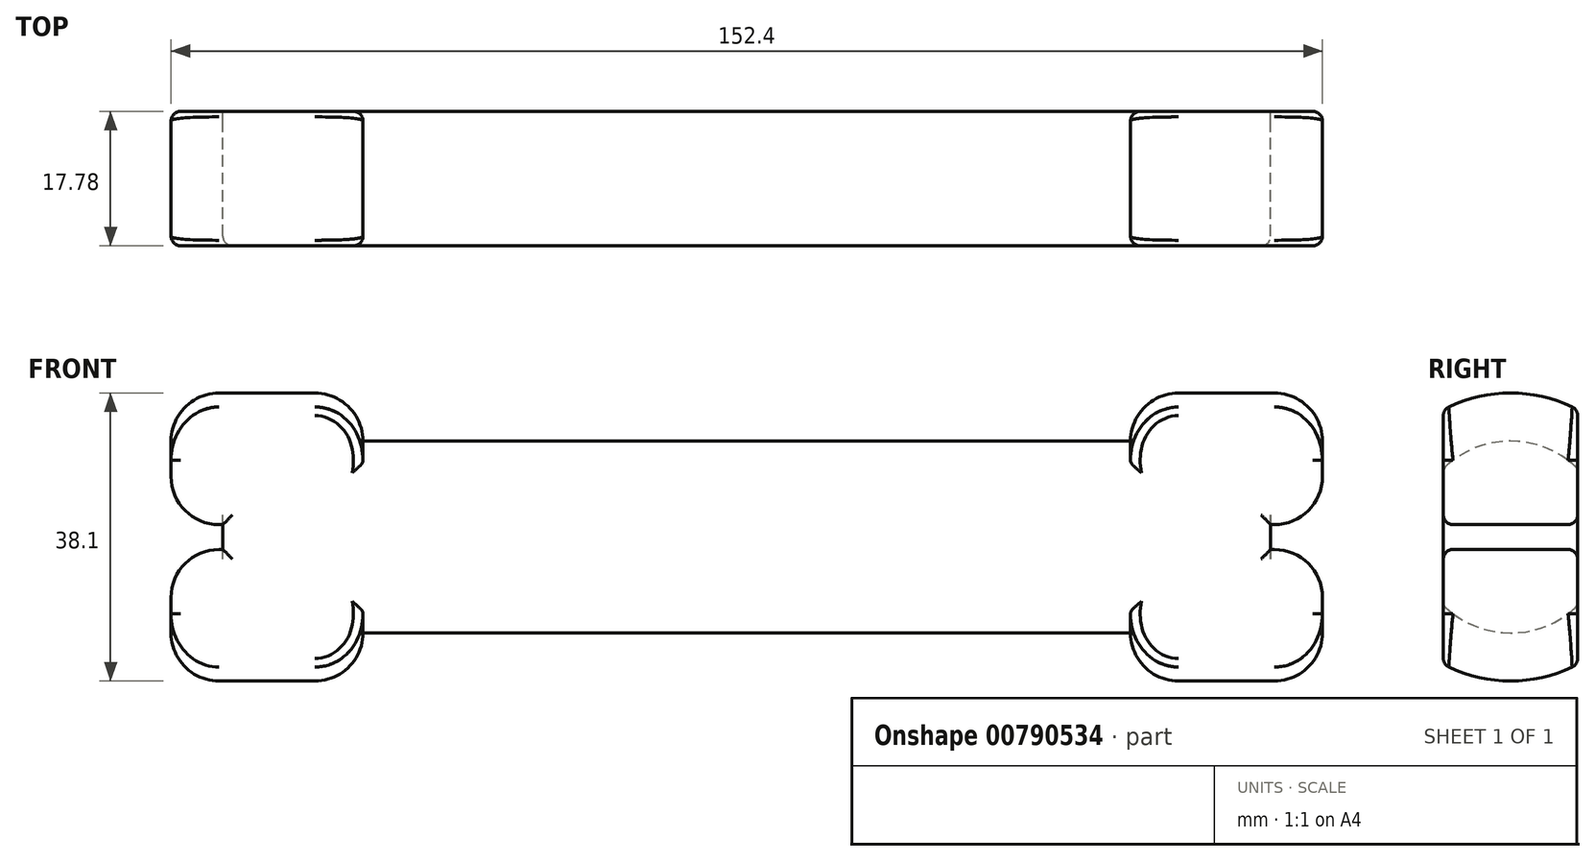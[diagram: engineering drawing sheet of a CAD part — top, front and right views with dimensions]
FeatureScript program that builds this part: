
annotation { "Feature Type Name" : "Feature", "Feature Type Description" : "" }
export const myFeature = defineFeature(function(context is Context, id is Id, definition is map)
    precondition{}
    {
        {
            var Q0;
            Q0=qCreatedBy(makeId("Front.planeOp"),FACE);
            var sketch = newSketch(context, id + "F0", { "sketchPlane" : qUnion([Q0])});
            skLineSegment(sketch, "E0.bottom", {"start": v(0, 0) * mm, "end": v(50.8, 0) * mm});
            skLineSegment(sketch, "E0.top", {"start": v(0, 19.05) * mm, "end": v(50.8, 19.05) * mm});
            skLineSegment(sketch, "E0.left", {"start": v(0, 0) * mm, "end": v(0, 19.05) * mm});
            skLineSegment(sketch, "E0.right", {"start": v(50.8, 0) * mm, "end": v(50.8, 19.05) * mm});
            skLineSegment(sketch, "E1.bottom", {"start": v(50.8, 19.05) * mm, "end": v(76.2, 19.05) * mm});
            skLineSegment(sketch, "E1.top", {"start": v(50.8, 0) * mm, "end": v(76.2, 0) * mm});
            skLineSegment(sketch, "E1.left", {"start": v(50.8, 19.05) * mm, "end": v(50.8, 0) * mm});
            skLineSegment(sketch, "E1.right", {"start": v(76.2, 19.05) * mm, "end": v(76.2, 0) * mm});
            skLineSegment(sketch, "E2.bottom", {"start": v(50.8, 19.05) * mm, "end": v(0, 19.05) * mm});
            skLineSegment(sketch, "E2.top", {"start": v(50.8, 12.7) * mm, "end": v(0, 12.7) * mm});
            skLineSegment(sketch, "E2.left", {"start": v(50.8, 19.05) * mm, "end": v(50.8, 12.7) * mm});
            skLineSegment(sketch, "E2.right", {"start": v(0, 19.05) * mm, "end": v(0, 12.7) * mm});
            skSolve(sketch);
        }
        {
            var Q0;
            {var subQ0=sQuery(id+"F0.wireOp",EDGE,"E0.bottom");Q0=makeQuery(id+"F0.imprint","IMPRINT",FACE,{"disambiguationData":[TD([[makeQuery(id+"F0.imprint","IMPRINT",EDGE,{"derivedFrom":subQ0}),1.0]])]});}
            var Q1;
            {var subQ1=sQuery(id+"F0.wireOp",EDGE,"E1.bottom");Q1=makeQuery(id+"F0.imprint","IMPRINT",FACE,{"disambiguationData":[TD([[makeQuery(id+"F0.imprint","IMPRINT",EDGE,{"derivedFrom":subQ1}),-1.0]])]});}
            var Q2;
            Q2=sQuery(id+"F0.wireOp",EDGE,"E1.top");
            revolve(context, id + "F1", {"surfaceOperationType" : NewSurfaceOperationType.NEW, "entities" : qUnion([Q0, Q1]), "axis" : qUnion([Q2]), "revolveType" : RevolveType.FULL});
        }
        {
            var Q0;
            Q0=qCreatedBy(makeId("Right.planeOp"),FACE);
            var sketch = newSketch(context, id + "F2", { "sketchPlane" : qUnion([Q0])});
            skLineSegment(sketch, "E3.bottom", {"start": v(8.89, 25.95) * mm, "end": v(35.05, 25.95) * mm});
            skLineSegment(sketch, "E3.top", {"start": v(8.9, -27.68) * mm, "end": v(35.05, -27.68) * mm});
            skLineSegment(sketch, "E3.left", {"start": v(8.89, 25.95) * mm, "end": v(8.9, -27.68) * mm});
            skLineSegment(sketch, "E3.right", {"start": v(35.05, 25.95) * mm, "end": v(35.05, -27.68) * mm});
            skSolve(sketch);
        }
        {
            var Q0;
            Q0=makeQuery(id+"F2.imprint","IMPRINT",FACE,{"disambiguationData":[TD([[makeQuery(id+"F2.imprint","IMPRINT",EDGE,{"derivedFrom":sQuery(id+"F2.wireOp",EDGE,"E3.bottom")}),-1.0]])]});
            extrude(context, id + "F3", {"entities" : qUnion([Q0]), "endBound" : BoundingType.THROUGH_ALL, "depth" : 25.4 * mm, "offsetDistance" : 25.4 * mm});
        }
        {
            var Q0;
            Q0=makeQuery(id+"F3.opExtrude","SWEPT_BODY",BODY,{"disambiguationData":[OSD([sQuery(id+"F2.wireOp",EDGE,"E3.bottom"),sQuery(id+"F2.wireOp",EDGE,"E3.top"),sQuery(id+"F2.wireOp",EDGE,"E3.left"),sQuery(id+"F2.wireOp",EDGE,"E3.right")])]});
            var Q1;
            Q1=qCreatedBy(makeId("Front.planeOp"),FACE);
            mirror(context, id + "F4", {"entities" : qUnion([Q0]), "mirrorPlane" : qUnion([Q1])});
        }
        {
            var Q0;
            Q0=makeQuery(id+"F4.opPattern","COPY",BODY,{"derivedFrom":makeQuery(id+"F3.opExtrude","SWEPT_BODY",BODY,{"disambiguationData":[OSD([sQuery(id+"F2.wireOp",EDGE,"E3.bottom"),sQuery(id+"F2.wireOp",EDGE,"E3.top"),sQuery(id+"F2.wireOp",EDGE,"E3.left"),sQuery(id+"F2.wireOp",EDGE,"E3.right")])]}),"instanceName":"1"});
            var Q1;
            Q1=makeQuery(id+"F3.opExtrude","SWEPT_BODY",BODY,{"disambiguationData":[OSD([sQuery(id+"F2.wireOp",EDGE,"E3.bottom"),sQuery(id+"F2.wireOp",EDGE,"E3.top"),sQuery(id+"F2.wireOp",EDGE,"E3.left"),sQuery(id+"F2.wireOp",EDGE,"E3.right")])]});
            var Q2;
            Q2=makeQuery(id+"F1.opRevolve","SWEPT_BODY",BODY,{"disambiguationData":[OSD([sQuery(id+"F0.wireOp",EDGE,"E0.bottom"),sQuery(id+"F0.wireOp",EDGE,"E0.left"),sQuery(id+"F0.wireOp",EDGE,"E0.right"),sQuery(id+"F0.wireOp",EDGE,"E1.bottom"),sQuery(id+"F0.wireOp",EDGE,"E1.top"),sQuery(id+"F0.wireOp",EDGE,"E1.right"),sQuery(id+"F0.wireOp",EDGE,"E2.top")])]});
            booleanBodies(context, id + "F5", {"operationType" : BooleanOperationType.SUBTRACTION, "tools" : qUnion([Q0, Q1]), "targets" : qUnion([Q2])});
        }
        {
            var Q0;
            Q0=qCreatedBy(makeId("Front.planeOp"),FACE);
            var sketch = newSketch(context, id + "F6", { "sketchPlane" : qUnion([Q0])});
            skLineSegment(sketch, "E4.bottom", {"start": v(69.35, 0) * mm, "end": v(81.98, 0) * mm});
            skLineSegment(sketch, "E4.top", {"start": v(69.35, 1.65) * mm, "end": v(81.98, 1.65) * mm});
            skLineSegment(sketch, "E4.left", {"start": v(69.35, 0) * mm, "end": v(69.35, 1.65) * mm});
            skLineSegment(sketch, "E4.right", {"start": v(81.98, 0) * mm, "end": v(81.98, 1.65) * mm});
            skLineSegment(sketch, "E5.MirrorCS", {"start": v(81.98, 0) * mm, "end": v(81.98, -1.65) * mm});
            skLineSegment(sketch, "E6.MirrorCS", {"start": v(69.35, -1.65) * mm, "end": v(81.98, -1.65) * mm});
            skLineSegment(sketch, "E7.MirrorCS", {"start": v(69.35, 0) * mm, "end": v(69.35, -1.65) * mm});
            skSolve(sketch);
        }
        {
            var Q0;
            Q0=makeQuery(id+"F6.imprint","IMPRINT",FACE,{"disambiguationData":[TD([[makeQuery(id+"F6.imprint","IMPRINT",EDGE,{"derivedFrom":sQuery(id+"F6.wireOp",EDGE,"E4.bottom")}),1.0]])]});
            var Q1;
            Q1=makeQuery(id+"F6.imprint","IMPRINT",FACE,{"disambiguationData":[TD([[makeQuery(id+"F6.imprint","IMPRINT",EDGE,{"derivedFrom":sQuery(id+"F6.wireOp",EDGE,"E4.bottom")}),-1.0]])]});
            extrude(context, id + "F7", {"entities" : qUnion([Q0, Q1]), "operationType" : NewBodyOperationType.REMOVE, "endBound" : BoundingType.THROUGH_ALL, "depth" : 25.4 * mm, "offsetDistance" : 25.4 * mm, "hasSecondDirection" : true, "secondDirectionOppositeDirection" : true, "secondDirectionDepth" : 25.4 * mm});
        }
        {
            var Q0;
            Q0=makeQuery(id+"F7.boolean.opBoolean","INTERSECT",EDGE,{"derivedFrom":[makeQuery(id+"F1.opRevolve","SWEPT_FACE",FACE,{"disambiguationData":[OSD([sQuery(id+"F0.wireOp",EDGE,"E1.right")])]}),makeQuery(id+"F7.opExtrude","SWEPT_FACE",FACE,{"disambiguationData":[OSD([sQuery(id+"F6.wireOp",EDGE,"E4.top")])]})]});
            var Q1;
            Q1=makeQuery(id+"F7.boolean.opBoolean","INTERSECT",EDGE,{"derivedFrom":[makeQuery(id+"F1.opRevolve","SWEPT_FACE",FACE,{"disambiguationData":[OSD([sQuery(id+"F0.wireOp",EDGE,"E1.right")])]}),makeQuery(id+"F7.opExtrude","SWEPT_FACE",FACE,{"disambiguationData":[OSD([sQuery(id+"F6.wireOp",EDGE,"E6.MirrorCS")])]})]});
            var Q2;
            Q2=makeQuery(id+"F5.opBoolean","SPLIT",EDGE,{"disambiguationData":[OD(1.0)],"derivedFrom":makeQuery(id+"F1.opRevolve","SWEPT_EDGE",EDGE,{"disambiguationData":[OSD([sQuery(id+"F0.wireOp",EDGE,"E1.bottom"),sQuery(id+"F0.wireOp",EDGE,"E1.right")])]})});
            var Q3;
            Q3=makeQuery(id+"F5.opBoolean","SPLIT",EDGE,{"disambiguationData":[OD(0.0)],"derivedFrom":makeQuery(id+"F1.opRevolve","SWEPT_EDGE",EDGE,{"disambiguationData":[OSD([sQuery(id+"F0.wireOp",EDGE,"E1.bottom"),sQuery(id+"F0.wireOp",EDGE,"E1.right")])]})});
            var Q4;
            Q4=makeQuery(id+"F5.opBoolean","SPLIT",EDGE,{"disambiguationData":[OD(1.0)],"derivedFrom":makeQuery(id+"F1.opRevolve","SWEPT_EDGE",EDGE,{"disambiguationData":[OSD([sQuery(id+"F0.wireOp",EDGE,"E0.top"),sQuery(id+"F0.wireOp",EDGE,"E0.right"),sQuery(id+"F0.wireOp",EDGE,"E1.bottom")])]})});
            var Q5;
            Q5=makeQuery(id+"F5.opBoolean","SPLIT",EDGE,{"disambiguationData":[OD(0.0)],"derivedFrom":makeQuery(id+"F1.opRevolve","SWEPT_EDGE",EDGE,{"disambiguationData":[OSD([sQuery(id+"F0.wireOp",EDGE,"E0.top"),sQuery(id+"F0.wireOp",EDGE,"E0.right"),sQuery(id+"F0.wireOp",EDGE,"E1.bottom")])]})});
            fillet(context, id + "F8", {"entities" : qUnion([Q0, Q1, Q2, Q3, Q4, Q5]), "radius" : 6.35 * mm, "tangentPropagation" : true, "allowEdgeOverflow" : false});
        }
        {
            var Q0;
            Q0=makeQuery(id+"F1.opRevolve","SWEPT_BODY",BODY,{"disambiguationData":[OSD([sQuery(id+"F0.wireOp",EDGE,"E0.bottom"),sQuery(id+"F0.wireOp",EDGE,"E0.left"),sQuery(id+"F0.wireOp",EDGE,"E0.right"),sQuery(id+"F0.wireOp",EDGE,"E1.bottom"),sQuery(id+"F0.wireOp",EDGE,"E1.top"),sQuery(id+"F0.wireOp",EDGE,"E1.right"),sQuery(id+"F0.wireOp",EDGE,"E2.top")])]});
            var Q1;
            Q1=makeQuery(id+"F1.opRevolve","SWEPT_FACE",FACE,{"disambiguationData":[OSD([sQuery(id+"F0.wireOp",EDGE,"E0.left")])]});
            mirror(context, id + "F9", {"operationType" : NewBodyOperationType.ADD, "entities" : qUnion([Q0]), "mirrorPlane" : qUnion([Q1])});
        }
        {
            var Q0;
            {var subQ0=makeQuery(id+"F5.opBoolean","INTERSECT",EDGE,{"disambiguationData":[OD(0.0)],"derivedFrom":[makeQuery(id+"F1.opRevolve","SWEPT_FACE",FACE,{"disambiguationData":[OSD([sQuery(id+"F0.wireOp",EDGE,"E2.top")])]}),makeQuery(id+"F4.opPattern","COPY",FACE,{"derivedFrom":makeQuery(id+"F3.opExtrude","SWEPT_FACE",FACE,{"disambiguationData":[OSD([sQuery(id+"F2.wireOp",EDGE,"E3.left")])]}),"instanceName":"1"})]});Q0=makeQuery(id+"F9.boolean.opBoolean","MERGE",EDGE,{"derivedFrom":[subQ0,makeQuery(id+"F9.opPattern","COPY",EDGE,{"derivedFrom":subQ0,"instanceName":"1"})]});}
            var Q1;
            Q1=makeQuery(id+"F9.opPattern","COPY",EDGE,{"derivedFrom":makeQuery(id+"F8.opFillet","BLEND_EDGE",EDGE,{"blendedFrom":[makeQuery(id+"F5.opBoolean","SPLIT",EDGE,{"disambiguationData":[OD(0.0)],"derivedFrom":makeQuery(id+"F1.opRevolve","SWEPT_EDGE",EDGE,{"disambiguationData":[OSD([sQuery(id+"F0.wireOp",EDGE,"E0.top"),sQuery(id+"F0.wireOp",EDGE,"E0.right"),sQuery(id+"F0.wireOp",EDGE,"E1.bottom")])]})}),makeQuery(id+"F5.opBoolean","COPY",FACE,{"derivedFrom":makeQuery(id+"F4.opPattern","COPY",FACE,{"derivedFrom":makeQuery(id+"F3.opExtrude","SWEPT_FACE",FACE,{"disambiguationData":[OSD([sQuery(id+"F2.wireOp",EDGE,"E3.left")])]}),"instanceName":"1"})})],"blendedInto":[makeQuery(id+"F5.opBoolean","COPY",FACE,{"derivedFrom":makeQuery(id+"F4.opPattern","COPY",FACE,{"derivedFrom":makeQuery(id+"F3.opExtrude","SWEPT_FACE",FACE,{"disambiguationData":[OSD([sQuery(id+"F2.wireOp",EDGE,"E3.left")])]}),"instanceName":"1"})})]}),"instanceName":"1"});
            var Q2;
            Q2=makeQuery(id+"F9.opPattern","COPY",EDGE,{"derivedFrom":makeQuery(id+"F5.opBoolean","INTERSECT",EDGE,{"disambiguationData":[OD(0.0)],"derivedFrom":[makeQuery(id+"F1.opRevolve","SWEPT_FACE",FACE,{"disambiguationData":[OSD([sQuery(id+"F0.wireOp",EDGE,"E1.bottom")])]}),makeQuery(id+"F4.opPattern","COPY",FACE,{"derivedFrom":makeQuery(id+"F3.opExtrude","SWEPT_FACE",FACE,{"disambiguationData":[OSD([sQuery(id+"F2.wireOp",EDGE,"E3.left")])]}),"instanceName":"1"})]}),"instanceName":"1"});
            var Q3;
            Q3=makeQuery(id+"F9.opPattern","COPY",EDGE,{"derivedFrom":makeQuery(id+"F8.opFillet","BLEND_EDGE",EDGE,{"blendedFrom":[makeQuery(id+"F5.opBoolean","SPLIT",EDGE,{"disambiguationData":[OD(0.0)],"derivedFrom":makeQuery(id+"F1.opRevolve","SWEPT_EDGE",EDGE,{"disambiguationData":[OSD([sQuery(id+"F0.wireOp",EDGE,"E1.bottom"),sQuery(id+"F0.wireOp",EDGE,"E1.right")])]})}),makeQuery(id+"F5.opBoolean","COPY",FACE,{"derivedFrom":makeQuery(id+"F4.opPattern","COPY",FACE,{"derivedFrom":makeQuery(id+"F3.opExtrude","SWEPT_FACE",FACE,{"disambiguationData":[OSD([sQuery(id+"F2.wireOp",EDGE,"E3.left")])]}),"instanceName":"1"})})],"blendedInto":[makeQuery(id+"F5.opBoolean","COPY",FACE,{"derivedFrom":makeQuery(id+"F4.opPattern","COPY",FACE,{"derivedFrom":makeQuery(id+"F3.opExtrude","SWEPT_FACE",FACE,{"disambiguationData":[OSD([sQuery(id+"F2.wireOp",EDGE,"E3.left")])]}),"instanceName":"1"})})]}),"instanceName":"1"});
            var Q4;
            Q4=makeQuery(id+"F9.opPattern","COPY",EDGE,{"derivedFrom":makeQuery(id+"F8.opFillet","BLEND_EDGE",EDGE,{"blendedFrom":[makeQuery(id+"F7.boolean.opBoolean","INTERSECT",EDGE,{"derivedFrom":[makeQuery(id+"F1.opRevolve","SWEPT_FACE",FACE,{"disambiguationData":[OSD([sQuery(id+"F0.wireOp",EDGE,"E1.right")])]}),makeQuery(id+"F7.opExtrude","SWEPT_FACE",FACE,{"disambiguationData":[OSD([sQuery(id+"F6.wireOp",EDGE,"E6.MirrorCS")])]})]}),makeQuery(id+"F5.opBoolean","COPY",FACE,{"derivedFrom":makeQuery(id+"F4.opPattern","COPY",FACE,{"derivedFrom":makeQuery(id+"F3.opExtrude","SWEPT_FACE",FACE,{"disambiguationData":[OSD([sQuery(id+"F2.wireOp",EDGE,"E3.left")])]}),"instanceName":"1"})})],"blendedInto":[makeQuery(id+"F5.opBoolean","COPY",FACE,{"derivedFrom":makeQuery(id+"F4.opPattern","COPY",FACE,{"derivedFrom":makeQuery(id+"F3.opExtrude","SWEPT_FACE",FACE,{"disambiguationData":[OSD([sQuery(id+"F2.wireOp",EDGE,"E3.left")])]}),"instanceName":"1"})})]}),"instanceName":"1"});
            var Q5;
            Q5=makeQuery(id+"F9.opPattern","COPY",EDGE,{"derivedFrom":makeQuery(id+"F7.boolean.opBoolean","INTERSECT",EDGE,{"derivedFrom":[makeQuery(id+"F5.opBoolean","COPY",FACE,{"derivedFrom":makeQuery(id+"F4.opPattern","COPY",FACE,{"derivedFrom":makeQuery(id+"F3.opExtrude","SWEPT_FACE",FACE,{"disambiguationData":[OSD([sQuery(id+"F2.wireOp",EDGE,"E3.left")])]}),"instanceName":"1"})}),makeQuery(id+"F7.opExtrude","SWEPT_FACE",FACE,{"disambiguationData":[OSD([sQuery(id+"F6.wireOp",EDGE,"E4.left"),sQuery(id+"F6.wireOp",EDGE,"E7.MirrorCS")])]})]}),"instanceName":"1"});
            var Q6;
            Q6=makeQuery(id+"F9.opPattern","COPY",EDGE,{"derivedFrom":makeQuery(id+"F8.opFillet","BLEND_EDGE",EDGE,{"blendedFrom":[makeQuery(id+"F7.boolean.opBoolean","INTERSECT",EDGE,{"derivedFrom":[makeQuery(id+"F1.opRevolve","SWEPT_FACE",FACE,{"disambiguationData":[OSD([sQuery(id+"F0.wireOp",EDGE,"E1.right")])]}),makeQuery(id+"F7.opExtrude","SWEPT_FACE",FACE,{"disambiguationData":[OSD([sQuery(id+"F6.wireOp",EDGE,"E4.top")])]})]}),makeQuery(id+"F5.opBoolean","COPY",FACE,{"derivedFrom":makeQuery(id+"F4.opPattern","COPY",FACE,{"derivedFrom":makeQuery(id+"F3.opExtrude","SWEPT_FACE",FACE,{"disambiguationData":[OSD([sQuery(id+"F2.wireOp",EDGE,"E3.left")])]}),"instanceName":"1"})})],"blendedInto":[makeQuery(id+"F5.opBoolean","COPY",FACE,{"derivedFrom":makeQuery(id+"F4.opPattern","COPY",FACE,{"derivedFrom":makeQuery(id+"F3.opExtrude","SWEPT_FACE",FACE,{"disambiguationData":[OSD([sQuery(id+"F2.wireOp",EDGE,"E3.left")])]}),"instanceName":"1"})})]}),"instanceName":"1"});
            var Q7;
            {var subQ0=makeQuery(id+"F5.opBoolean","INTERSECT",EDGE,{"disambiguationData":[OD(1.0)],"derivedFrom":[makeQuery(id+"F1.opRevolve","SWEPT_FACE",FACE,{"disambiguationData":[OSD([sQuery(id+"F0.wireOp",EDGE,"E2.top")])]}),makeQuery(id+"F4.opPattern","COPY",FACE,{"derivedFrom":makeQuery(id+"F3.opExtrude","SWEPT_FACE",FACE,{"disambiguationData":[OSD([sQuery(id+"F2.wireOp",EDGE,"E3.left")])]}),"instanceName":"1"})]});Q7=makeQuery(id+"F9.boolean.opBoolean","MERGE",EDGE,{"derivedFrom":[subQ0,makeQuery(id+"F9.opPattern","COPY",EDGE,{"derivedFrom":subQ0,"instanceName":"1"})]});}
            var Q8;
            Q8=makeQuery(id+"F8.opFillet","BLEND_EDGE",EDGE,{"blendedFrom":[makeQuery(id+"F5.opBoolean","SPLIT",EDGE,{"disambiguationData":[OD(0.0)],"derivedFrom":makeQuery(id+"F1.opRevolve","SWEPT_EDGE",EDGE,{"disambiguationData":[OSD([sQuery(id+"F0.wireOp",EDGE,"E0.top"),sQuery(id+"F0.wireOp",EDGE,"E0.right"),sQuery(id+"F0.wireOp",EDGE,"E1.bottom")])]})}),makeQuery(id+"F5.opBoolean","COPY",FACE,{"derivedFrom":makeQuery(id+"F4.opPattern","COPY",FACE,{"derivedFrom":makeQuery(id+"F3.opExtrude","SWEPT_FACE",FACE,{"disambiguationData":[OSD([sQuery(id+"F2.wireOp",EDGE,"E3.left")])]}),"instanceName":"1"})})],"blendedInto":[makeQuery(id+"F5.opBoolean","COPY",FACE,{"derivedFrom":makeQuery(id+"F4.opPattern","COPY",FACE,{"derivedFrom":makeQuery(id+"F3.opExtrude","SWEPT_FACE",FACE,{"disambiguationData":[OSD([sQuery(id+"F2.wireOp",EDGE,"E3.left")])]}),"instanceName":"1"})})]});
            var Q9;
            Q9=makeQuery(id+"F5.opBoolean","INTERSECT",EDGE,{"disambiguationData":[OD(0.0)],"derivedFrom":[makeQuery(id+"F1.opRevolve","SWEPT_FACE",FACE,{"disambiguationData":[OSD([sQuery(id+"F0.wireOp",EDGE,"E1.bottom")])]}),makeQuery(id+"F4.opPattern","COPY",FACE,{"derivedFrom":makeQuery(id+"F3.opExtrude","SWEPT_FACE",FACE,{"disambiguationData":[OSD([sQuery(id+"F2.wireOp",EDGE,"E3.left")])]}),"instanceName":"1"})]});
            var Q10;
            Q10=makeQuery(id+"F7.boolean.opBoolean","INTERSECT",EDGE,{"derivedFrom":[makeQuery(id+"F5.opBoolean","COPY",FACE,{"derivedFrom":makeQuery(id+"F4.opPattern","COPY",FACE,{"derivedFrom":makeQuery(id+"F3.opExtrude","SWEPT_FACE",FACE,{"disambiguationData":[OSD([sQuery(id+"F2.wireOp",EDGE,"E3.left")])]}),"instanceName":"1"})}),makeQuery(id+"F7.opExtrude","SWEPT_FACE",FACE,{"disambiguationData":[OSD([sQuery(id+"F6.wireOp",EDGE,"E4.left"),sQuery(id+"F6.wireOp",EDGE,"E7.MirrorCS")])]})]});
            var Q11;
            Q11=makeQuery(id+"F8.opFillet","BLEND_EDGE",EDGE,{"blendedFrom":[makeQuery(id+"F7.boolean.opBoolean","INTERSECT",EDGE,{"derivedFrom":[makeQuery(id+"F1.opRevolve","SWEPT_FACE",FACE,{"disambiguationData":[OSD([sQuery(id+"F0.wireOp",EDGE,"E1.right")])]}),makeQuery(id+"F7.opExtrude","SWEPT_FACE",FACE,{"disambiguationData":[OSD([sQuery(id+"F6.wireOp",EDGE,"E4.top")])]})]}),makeQuery(id+"F5.opBoolean","COPY",FACE,{"derivedFrom":makeQuery(id+"F4.opPattern","COPY",FACE,{"derivedFrom":makeQuery(id+"F3.opExtrude","SWEPT_FACE",FACE,{"disambiguationData":[OSD([sQuery(id+"F2.wireOp",EDGE,"E3.left")])]}),"instanceName":"1"})})],"blendedInto":[makeQuery(id+"F5.opBoolean","COPY",FACE,{"derivedFrom":makeQuery(id+"F4.opPattern","COPY",FACE,{"derivedFrom":makeQuery(id+"F3.opExtrude","SWEPT_FACE",FACE,{"disambiguationData":[OSD([sQuery(id+"F2.wireOp",EDGE,"E3.left")])]}),"instanceName":"1"})})]});
            var Q12;
            {var subQ0=makeQuery(id+"F5.opBoolean","INTERSECT",EDGE,{"disambiguationData":[OD(0.0)],"derivedFrom":[makeQuery(id+"F1.opRevolve","SWEPT_FACE",FACE,{"disambiguationData":[OSD([sQuery(id+"F0.wireOp",EDGE,"E2.top")])]}),makeQuery(id+"F3.opExtrude","SWEPT_FACE",FACE,{"disambiguationData":[OSD([sQuery(id+"F2.wireOp",EDGE,"E3.left")])]})]});Q12=makeQuery(id+"F9.boolean.opBoolean","MERGE",EDGE,{"derivedFrom":[subQ0,makeQuery(id+"F9.opPattern","COPY",EDGE,{"derivedFrom":subQ0,"instanceName":"1"})]});}
            var Q13;
            {var subQ0=makeQuery(id+"F5.opBoolean","INTERSECT",EDGE,{"disambiguationData":[OD(1.0)],"derivedFrom":[makeQuery(id+"F1.opRevolve","SWEPT_FACE",FACE,{"disambiguationData":[OSD([sQuery(id+"F0.wireOp",EDGE,"E2.top")])]}),makeQuery(id+"F3.opExtrude","SWEPT_FACE",FACE,{"disambiguationData":[OSD([sQuery(id+"F2.wireOp",EDGE,"E3.left")])]})]});Q13=makeQuery(id+"F9.boolean.opBoolean","MERGE",EDGE,{"derivedFrom":[subQ0,makeQuery(id+"F9.opPattern","COPY",EDGE,{"derivedFrom":subQ0,"instanceName":"1"})]});}
            var Q14;
            Q14=makeQuery(id+"F8.opFillet","BLEND_EDGE",EDGE,{"blendedFrom":[makeQuery(id+"F5.opBoolean","SPLIT",EDGE,{"disambiguationData":[OD(1.0)],"derivedFrom":makeQuery(id+"F1.opRevolve","SWEPT_EDGE",EDGE,{"disambiguationData":[OSD([sQuery(id+"F0.wireOp",EDGE,"E1.bottom"),sQuery(id+"F0.wireOp",EDGE,"E1.right")])]})}),makeQuery(id+"F5.opBoolean","COPY",FACE,{"derivedFrom":makeQuery(id+"F3.opExtrude","SWEPT_FACE",FACE,{"disambiguationData":[OSD([sQuery(id+"F2.wireOp",EDGE,"E3.left")])]})})],"blendedInto":[makeQuery(id+"F5.opBoolean","COPY",FACE,{"derivedFrom":makeQuery(id+"F3.opExtrude","SWEPT_FACE",FACE,{"disambiguationData":[OSD([sQuery(id+"F2.wireOp",EDGE,"E3.left")])]})})]});
            var Q15;
            Q15=makeQuery(id+"F8.opFillet","BLEND_EDGE",EDGE,{"blendedFrom":[makeQuery(id+"F5.opBoolean","SPLIT",EDGE,{"disambiguationData":[OD(0.0)],"derivedFrom":makeQuery(id+"F1.opRevolve","SWEPT_EDGE",EDGE,{"disambiguationData":[OSD([sQuery(id+"F0.wireOp",EDGE,"E1.bottom"),sQuery(id+"F0.wireOp",EDGE,"E1.right")])]})}),makeQuery(id+"F5.opBoolean","COPY",FACE,{"derivedFrom":makeQuery(id+"F3.opExtrude","SWEPT_FACE",FACE,{"disambiguationData":[OSD([sQuery(id+"F2.wireOp",EDGE,"E3.left")])]})})],"blendedInto":[makeQuery(id+"F5.opBoolean","COPY",FACE,{"derivedFrom":makeQuery(id+"F3.opExtrude","SWEPT_FACE",FACE,{"disambiguationData":[OSD([sQuery(id+"F2.wireOp",EDGE,"E3.left")])]})})]});
            var Q16;
            Q16=makeQuery(id+"F9.opPattern","COPY",EDGE,{"derivedFrom":makeQuery(id+"F8.opFillet","BLEND_EDGE",EDGE,{"blendedFrom":[makeQuery(id+"F5.opBoolean","SPLIT",EDGE,{"disambiguationData":[OD(1.0)],"derivedFrom":makeQuery(id+"F1.opRevolve","SWEPT_EDGE",EDGE,{"disambiguationData":[OSD([sQuery(id+"F0.wireOp",EDGE,"E1.bottom"),sQuery(id+"F0.wireOp",EDGE,"E1.right")])]})}),makeQuery(id+"F5.opBoolean","COPY",FACE,{"derivedFrom":makeQuery(id+"F3.opExtrude","SWEPT_FACE",FACE,{"disambiguationData":[OSD([sQuery(id+"F2.wireOp",EDGE,"E3.left")])]})})],"blendedInto":[makeQuery(id+"F5.opBoolean","COPY",FACE,{"derivedFrom":makeQuery(id+"F3.opExtrude","SWEPT_FACE",FACE,{"disambiguationData":[OSD([sQuery(id+"F2.wireOp",EDGE,"E3.left")])]})})]}),"instanceName":"1"});
            var Q17;
            Q17=makeQuery(id+"F9.opPattern","COPY",EDGE,{"derivedFrom":makeQuery(id+"F8.opFillet","BLEND_EDGE",EDGE,{"blendedFrom":[makeQuery(id+"F5.opBoolean","SPLIT",EDGE,{"disambiguationData":[OD(0.0)],"derivedFrom":makeQuery(id+"F1.opRevolve","SWEPT_EDGE",EDGE,{"disambiguationData":[OSD([sQuery(id+"F0.wireOp",EDGE,"E1.bottom"),sQuery(id+"F0.wireOp",EDGE,"E1.right")])]})}),makeQuery(id+"F5.opBoolean","COPY",FACE,{"derivedFrom":makeQuery(id+"F3.opExtrude","SWEPT_FACE",FACE,{"disambiguationData":[OSD([sQuery(id+"F2.wireOp",EDGE,"E3.left")])]})})],"blendedInto":[makeQuery(id+"F5.opBoolean","COPY",FACE,{"derivedFrom":makeQuery(id+"F3.opExtrude","SWEPT_FACE",FACE,{"disambiguationData":[OSD([sQuery(id+"F2.wireOp",EDGE,"E3.left")])]})})]}),"instanceName":"1"});
            fillet(context, id + "F10", {"entities" : qUnion([Q0, Q1, Q2, Q3, Q4, Q5, Q6, Q7, Q8, Q9, Q10, Q11, Q12, Q13, Q14, Q15, Q16, Q17]), "radius" : 1.27 * mm, "tangentPropagation" : true, "allowEdgeOverflow" : false});
        }
    });
